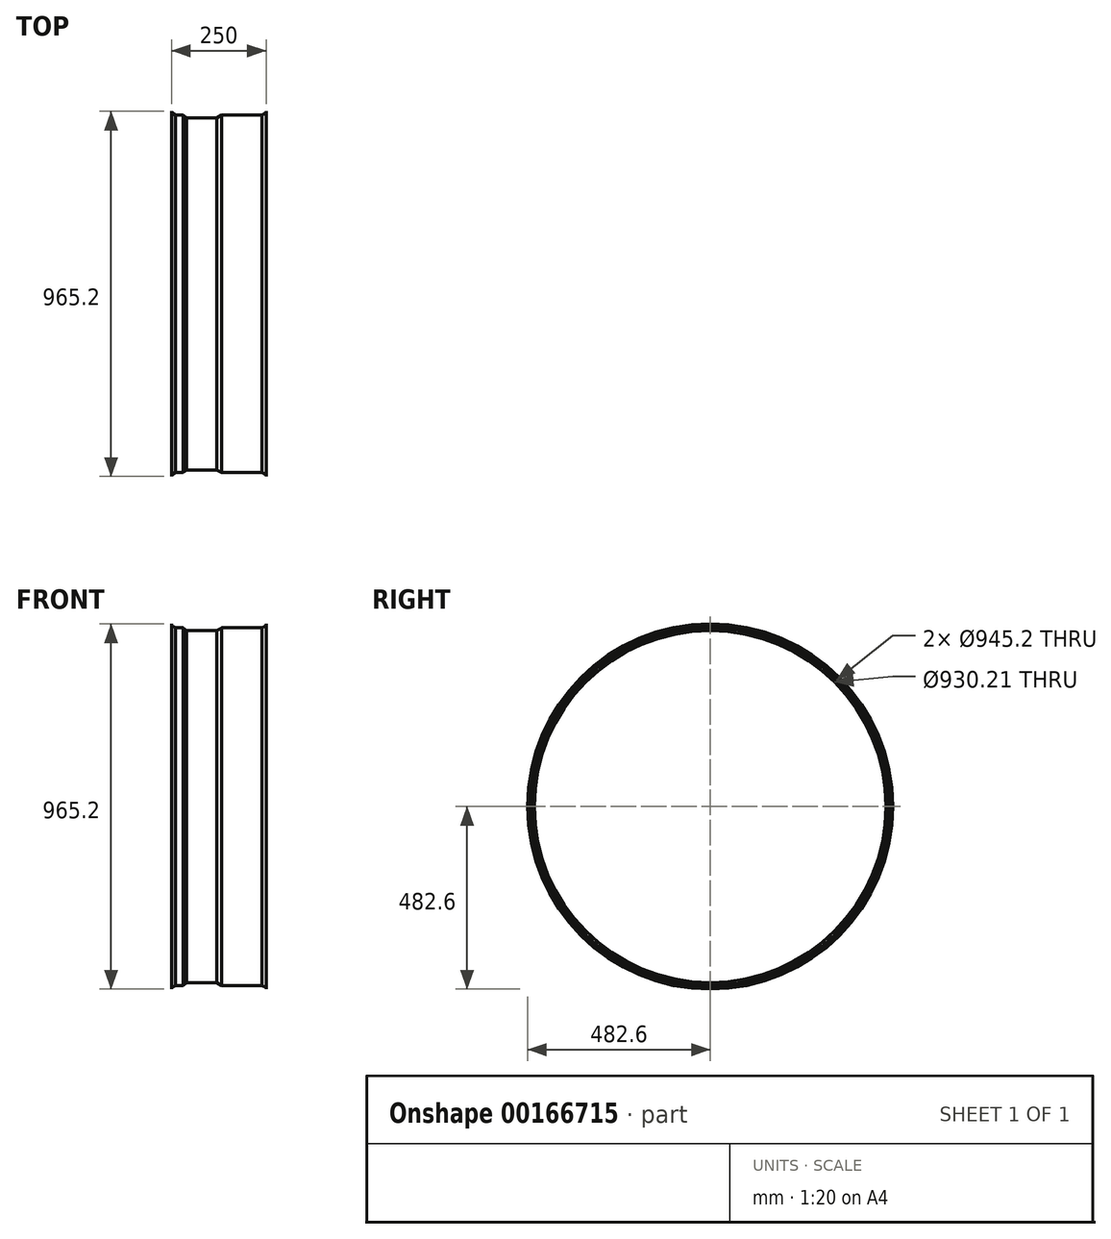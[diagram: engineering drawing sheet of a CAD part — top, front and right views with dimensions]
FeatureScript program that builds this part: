
annotation { "Feature Type Name" : "Feature", "Feature Type Description" : "" }
export const myFeature = defineFeature(function(context is Context, id is Id, definition is map)
    precondition{}
    {
        {
            var Q0;
            Q0=qCreatedBy(makeId("Front.planeOp"),FACE);
            var sketch = newSketch(context, id + "F0", { "sketchPlane" : qUnion([Q0])});
            skLineSegment(sketch, "E0", {"start": v(0, 482.6) * mm, "end": v(0, 478.6) * mm});
            skLineSegment(sketch, "E1", {"start": v(0, 478.6) * mm, "end": v(10.4, 472.6) * mm});
            skLineSegment(sketch, "E2", {"start": v(10.4, 472.6) * mm, "end": v(30.4, 472.6) * mm});
            skLineSegment(sketch, "E3", {"start": v(30.4, 472.6) * mm, "end": v(39.76, 465.1) * mm});
            skLineSegment(sketch, "E4", {"start": v(39.76, 465.1) * mm, "end": v(119.76, 465.1) * mm});
            skLineSegment(sketch, "E5", {"start": v(119.76, 465.1) * mm, "end": v(132.75, 472.6) * mm});
            skLineSegment(sketch, "E6", {"start": v(132.75, 472.6) * mm, "end": v(239.6, 472.6) * mm});
            skLineSegment(sketch, "E7", {"start": v(239.6, 472.6) * mm, "end": v(250, 478.6) * mm});
            skLineSegment(sketch, "E8", {"start": v(250, 478.6) * mm, "end": v(250, 482.6) * mm});
            skLineSegment(sketch, "E9", {"start": v(0, 0) * mm, "end": v(0, 52.54) * mm});
            skLineSegment(sketch, "E10", {"start": v(0, 482.6) * mm, "end": v(0, 482.6) * mm});
            skLineSegment(sketch, "E11", {"start": v(250, 482.6) * mm, "end": v(250, 482.6) * mm});
            skLineSegment(sketch, "E12", {"start": v(0, 0) * mm, "end": v(57.47, 0) * mm});
            skSolve(sketch);
        }
        {
            var Q0;
            Q0=makeQuery(id+"F0.imprint","IMPRINT",FACE,{"disambiguationData":[TD([[makeQuery(id+"F0.imprint","IMPRINT",EDGE,{"derivedFrom":sQuery(id+"F0.wireOp",EDGE,"E1")}),1.0]])]});
            var Q1;
            Q1=sQuery(id+"F0.wireOp",EDGE,"E12");
            revolve(context, id + "F1", {"entities" : qUnion([Q0]), "axis" : qUnion([Q1]), "revolveType" : RevolveType.FULL});
        }
    });
